# Revit family: Скамейка стальная «Вена» Арт 8313
name_source: partatom
category: Антураж
revit_build: Autodesk Revit 2018 (Build: 20180423_1000(x64)
units: mm (PartAtom-declared; Revit-internal decimal feet)

## family parameters
Всегда вертикально = Да
Источник визуального образа = Геометрия семейства
На основе рабочей плоскости = Нет
Общий = Нет
При загрузке вырезать с полостями = Нет
Точка расчета площади = Нет

## types (7) — shared parameters
URL = https://hobbyka.ru
Артикул товара = Арт. 8313
Группа модели = Садовые скамейки
Изготовитель = ООО «Хоббика»
Материал изделия = Сталь, дерево
Цвет лавки = Дерево
Цвет опоры = Сталь

## per-type parameters (varying)
| type | Версия 0,6 м (Кресло) | Версия 1,2 м | Версия 1,5 м | Версия 1,8 м | Версия 2,0 м (2 опоры) | Версия 2,0 м (3 опоры) | Версия 3,0 м (3 опоры) | Высота | Длина | Изображение типоразмера | Описание | Средняя опора | Ширина |
| Версия Кресло | Да | Нет | Нет | Нет | Нет | Нет | Нет | 840 мм | 600 мм | Скамейка стальная «Вена» Арт 8313 кресло.jpg | Скамейка стальная «Вена». Версия Кресло | Нет | 570 мм |
| Версия 1,2 м | Нет | Да | Нет | Нет | Да | Нет | Нет | 835 мм | 1200 мм | Скамейка стальная «Вена» Арт 8313 2 опоры.jpg | Скамейка стальная «Вена». Версия 1,2 м | Нет | 612 мм |
| Версия 1,5 м | Нет | Нет | Да | Нет | Да | Нет | Нет | 835 мм | 1500 мм | Скамейка стальная «Вена» Арт 8313 2 опоры.jpg | Скамейка стальная «Вена». Версия 1,5 м | Нет | 612 мм |
| Версия 1,8 м | Нет | Нет | Нет | Да | Да | Нет | Нет | 835 мм | 1800 мм | Скамейка стальная «Вена» Арт 8313 2 опоры.jpg | Скамейка стальная «Вена». Версия 1,8 м | Нет | 612 мм |
| Версия 3,0 м (3 опоры) | Нет | Нет | Нет | Нет | Да | Нет | Да | 835 мм | 2000 мм | Скамейка стальная «Вена» Арт 8313 2 опоры.jpg | Скамейка стальная «Вена». Версия 2,0 м (2 опоры) | Да | 612 мм |
| Версия 2,0 м (3 опоры) | Нет | Нет | Нет | Нет | Да | Да | Нет | 835 мм | 2000 мм | Скамейка стальная «Вена» Арт 8313 2 опоры.jpg | Скамейка стальная «Вена». Версия 2,0 м (2 опоры) | Да | 612 мм |
| Версия 2,0 м (2 опоры) | Нет | Нет | Нет | Нет | Да | Нет | Нет | 835 мм | 2000 мм | Скамейка стальная «Вена» Арт 8313 2 опоры.jpg | Скамейка стальная «Вена». Версия 2,0 м (2 опоры) | Нет | 612 мм |
